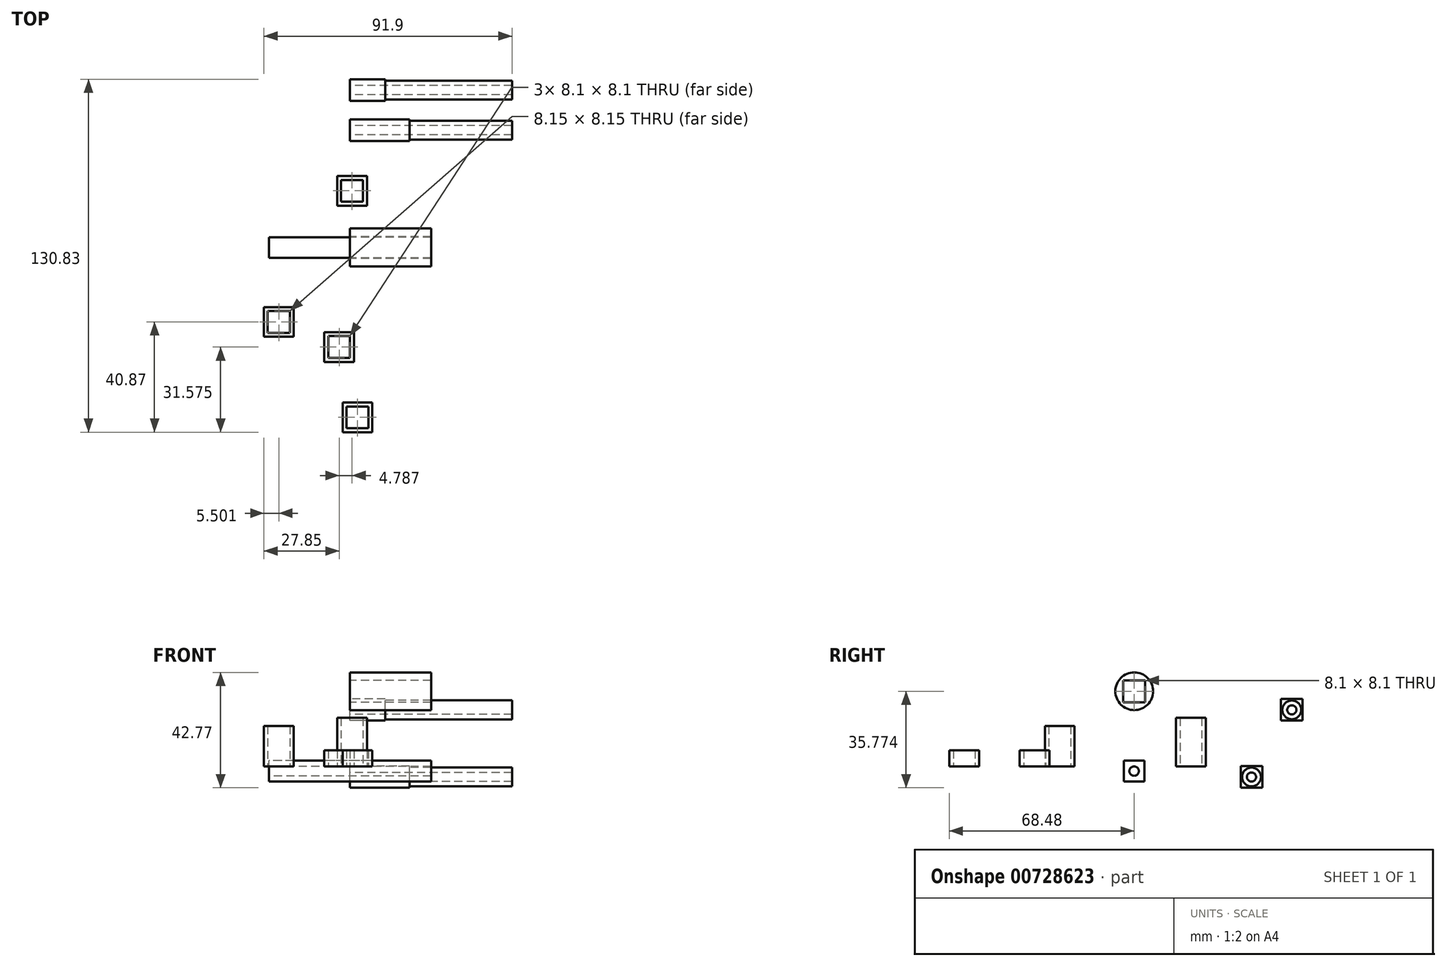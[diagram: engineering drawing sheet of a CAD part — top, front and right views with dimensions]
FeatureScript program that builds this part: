
annotation { "Feature Type Name" : "Feature", "Feature Type Description" : "" }
export const myFeature = defineFeature(function(context is Context, id is Id, definition is map)
    precondition{}
    {
        {
            var Q0;
            Q0=qCreatedBy(makeId("Right.planeOp"),FACE);
            var sketch = newSketch(context, id + "F0", { "sketchPlane" : qUnion([Q0])});
            skLineSegment(sketch, "E0.bottom", {"start": v(3.85, -3.85) * mm, "end": v(-3.85, -3.85) * mm});
            skLineSegment(sketch, "E0.top", {"start": v(3.85, 3.85) * mm, "end": v(-3.85, 3.85) * mm});
            skLineSegment(sketch, "E0.left", {"start": v(3.85, -3.85) * mm, "end": v(3.85, 3.85) * mm});
            skLineSegment(sketch, "E0.right", {"start": v(-3.85, -3.85) * mm, "end": v(-3.85, 3.85) * mm});
            skPoint(sketch, "E0.middle", {"position": v(0, 0) * mm});
            skCircle(sketch, "E1", {"center": v(0, 0) * mm, "radius": 1.75 * mm});
            skCircle(sketch, "E2", {"center": v(43.48, -2.18) * mm, "radius": 1.7 * mm});
            skLineSegment(sketch, "E3.bottom", {"start": v(47.48, -6.18) * mm, "end": v(39.48, -6.18) * mm});
            skLineSegment(sketch, "E3.top", {"start": v(47.48, 1.82) * mm, "end": v(39.48, 1.82) * mm});
            skLineSegment(sketch, "E3.left", {"start": v(47.48, -6.18) * mm, "end": v(47.48, 1.82) * mm});
            skLineSegment(sketch, "E3.right", {"start": v(39.48, -6.18) * mm, "end": v(39.48, 1.82) * mm});
            skCircle(sketch, "E4", {"center": v(58.4, 22.7) * mm, "radius": 1.7 * mm});
            skLineSegment(sketch, "E5.bottom", {"start": v(62.4, 18.7) * mm, "end": v(54.4, 18.7) * mm});
            skLineSegment(sketch, "E5.top", {"start": v(62.4, 26.7) * mm, "end": v(54.4, 26.7) * mm});
            skLineSegment(sketch, "E5.left", {"start": v(62.4, 18.7) * mm, "end": v(62.4, 26.7) * mm});
            skLineSegment(sketch, "E5.right", {"start": v(54.4, 18.7) * mm, "end": v(54.4, 26.7) * mm});
            skSolve(sketch);
        }
        {
            var Q0;
            Q0=makeQuery(id+"F0.imprint","IMPRINT",FACE,{"disambiguationData":[TD([[makeQuery(id+"F0.imprint","IMPRINT",EDGE,{"derivedFrom":sQuery(id+"F0.wireOp",EDGE,"E0.bottom")}),-1.0]])]});
            extrude(context, id + "F1", {"entities" : qUnion([Q0]), "endBound" : BoundingType.SYMMETRIC, "depth" : 60 * mm, "offsetDistance" : 25 * mm});
        }
        {
            var Q0;
            Q0=qCreatedBy(makeId("Right.planeOp"),FACE);
            var sketch = newSketch(context, id + "F2", { "sketchPlane" : qUnion([Q0])});
            skLineSegment(sketch, "E6.bottom", {"start": v(-32.8, 1.71) * mm, "end": v(-40.9, 1.71) * mm});
            skLineSegment(sketch, "E6.top", {"start": v(-32.8, 9.81) * mm, "end": v(-40.9, 9.81) * mm});
            skLineSegment(sketch, "E6.left", {"start": v(-32.8, 1.71) * mm, "end": v(-32.8, 9.81) * mm});
            skLineSegment(sketch, "E6.right", {"start": v(-40.9, 1.71) * mm, "end": v(-40.9, 9.81) * mm});
            skPoint(sketch, "E6.middle", {"position": v(-36.86, 5.76) * mm});
            skLineSegment(sketch, "E7.bottom", {"start": v(-42.36, 0.26) * mm, "end": v(-31.36, 0.26) * mm});
            skLineSegment(sketch, "E7.top", {"start": v(-42.36, 11.26) * mm, "end": v(-31.36, 11.26) * mm});
            skLineSegment(sketch, "E7.left", {"start": v(-42.36, 0.26) * mm, "end": v(-42.36, 11.26) * mm});
            skLineSegment(sketch, "E7.right", {"start": v(-31.36, 0.26) * mm, "end": v(-31.36, 11.26) * mm});
            skSolve(sketch);
        }
        {
            var Q0;
            Q0 = qSketchRegion(id + "F2", true);
            extrude(context, id + "F3", {"entities" : qUnion([Q0]), "depth" : 6 * mm, "offsetDistance" : 25 * mm});
        }
        {
            var Q0;
            Q0=qCreatedBy(makeId("Right.planeOp"),FACE);
            var sketch = newSketch(context, id + "F4", { "sketchPlane" : qUnion([Q0])});
            skLineSegment(sketch, "E8.bottom", {"start": v(25.07, -3.07) * mm, "end": v(16.97, -3.07) * mm});
            skLineSegment(sketch, "E8.top", {"start": v(25.07, 5.03) * mm, "end": v(16.97, 5.03) * mm});
            skLineSegment(sketch, "E8.left", {"start": v(25.07, -3.07) * mm, "end": v(25.07, 5.03) * mm});
            skLineSegment(sketch, "E8.right", {"start": v(16.97, -3.07) * mm, "end": v(16.97, 5.03) * mm});
            skPoint(sketch, "E8.middle", {"position": v(21.02, 0.98) * mm});
            skLineSegment(sketch, "E9.bottom", {"start": v(15.52, -4.52) * mm, "end": v(26.52, -4.52) * mm});
            skLineSegment(sketch, "E9.top", {"start": v(15.52, 6.48) * mm, "end": v(26.52, 6.48) * mm});
            skLineSegment(sketch, "E9.left", {"start": v(15.52, -4.52) * mm, "end": v(15.52, 6.48) * mm});
            skLineSegment(sketch, "E9.right", {"start": v(26.52, -4.52) * mm, "end": v(26.52, 6.48) * mm});
            skSolve(sketch);
        }
        {
            var Q0;
            Q0 = qSketchRegion(id + "F4", true);
            extrude(context, id + "F5", {"entities" : qUnion([Q0]), "depth" : 18 * mm, "offsetDistance" : 25 * mm});
        }
        {
            var Q0;
            Q0=qCreatedBy(makeId("Right.planeOp"),FACE);
            var sketch = newSketch(context, id + "F6", { "sketchPlane" : qUnion([Q0])});
            skLineSegment(sketch, "E10.bottom", {"start": v(-58.88, -5.07) * mm, "end": v(-66.98, -5.07) * mm});
            skLineSegment(sketch, "E10.top", {"start": v(-58.88, 3.03) * mm, "end": v(-66.98, 3.03) * mm});
            skLineSegment(sketch, "E10.left", {"start": v(-58.88, -5.07) * mm, "end": v(-58.88, 3.03) * mm});
            skLineSegment(sketch, "E10.right", {"start": v(-66.98, -5.07) * mm, "end": v(-66.98, 3.03) * mm});
            skPoint(sketch, "E10.middle", {"position": v(-62.93, -1.02) * mm});
            skLineSegment(sketch, "E11.bottom", {"start": v(-68.43, -6.52) * mm, "end": v(-57.43, -6.52) * mm});
            skLineSegment(sketch, "E11.top", {"start": v(-68.43, 4.48) * mm, "end": v(-57.43, 4.48) * mm});
            skLineSegment(sketch, "E11.left", {"start": v(-68.43, -6.52) * mm, "end": v(-68.43, 4.48) * mm});
            skLineSegment(sketch, "E11.right", {"start": v(-57.43, -6.52) * mm, "end": v(-57.43, 4.48) * mm});
            skSolve(sketch);
        }
        {
            var Q0;
            Q0 = qSketchRegion(id + "F6", true);
            extrude(context, id + "F7", {"entities" : qUnion([Q0]), "depth" : 6 * mm, "offsetDistance" : 25 * mm});
        }
        {
            var Q0;
            Q0=qCreatedBy(makeId("Right.planeOp"),FACE);
            var sketch = newSketch(context, id + "F8", { "sketchPlane" : qUnion([Q0])});
            skLineSegment(sketch, "E12.bottom", {"start": v(-23.48, 24.04) * mm, "end": v(-31.63, 24.04) * mm});
            skLineSegment(sketch, "E12.top", {"start": v(-23.48, 32.19) * mm, "end": v(-31.63, 32.19) * mm});
            skLineSegment(sketch, "E12.left", {"start": v(-23.48, 24.04) * mm, "end": v(-23.48, 32.19) * mm});
            skLineSegment(sketch, "E12.right", {"start": v(-31.63, 24.04) * mm, "end": v(-31.63, 32.19) * mm});
            skPoint(sketch, "E12.middle", {"position": v(-27.56, 28.11) * mm});
            skLineSegment(sketch, "E13.bottom", {"start": v(-22.06, 22.61) * mm, "end": v(-33.06, 22.61) * mm});
            skLineSegment(sketch, "E13.top", {"start": v(-22.06, 33.61) * mm, "end": v(-33.06, 33.61) * mm});
            skLineSegment(sketch, "E13.left", {"start": v(-22.06, 22.61) * mm, "end": v(-22.06, 33.61) * mm});
            skLineSegment(sketch, "E13.right", {"start": v(-33.06, 22.61) * mm, "end": v(-33.06, 33.61) * mm});
            skSolve(sketch);
        }
        {
            var Q0;
            Q0 = qSketchRegion(id + "F8", true);
            extrude(context, id + "F9", {"entities" : qUnion([Q0]), "depth" : 15 * mm, "offsetDistance" : 25 * mm});
        }
        {
            var Q0;
            Q0=qCreatedBy(makeId("Right.planeOp"),FACE);
            var sketch = newSketch(context, id + "F10", { "sketchPlane" : qUnion([Q0])});
            skCircle(sketch, "E14", {"center": v(43.48, -2.18) * mm, "radius": 1.7 * mm});
            skCircle(sketch, "E15", {"center": v(43.48, -2.18) * mm, "radius": 3.5 * mm});
            skCircle(sketch, "E16", {"center": v(58.4, 22.7) * mm, "radius": 1.7 * mm});
            skCircle(sketch, "E17", {"center": v(58.4, 22.7) * mm, "radius": 3.5 * mm});
            skSolve(sketch);
        }
        {
            var Q0;
            Q0=makeQuery(id+"F0.imprint","IMPRINT",FACE,{"disambiguationData":[TD([[makeQuery(id+"F0.imprint","IMPRINT",EDGE,{"derivedFrom":sQuery(id+"F0.wireOp",EDGE,"E2")}),-1.0]])]});
            extrude(context, id + "F11", {"entities" : qUnion([Q0]), "operationType" : NewBodyOperationType.ADD, "depth" : 22 * mm, "offsetDistance" : 25 * mm});
        }
        {
            var Q0;
            Q0=makeQuery(id+"F10.imprint","IMPRINT",FACE,{"disambiguationData":[TD([[makeQuery(id+"F10.imprint","IMPRINT",EDGE,{"derivedFrom":sQuery(id+"F10.wireOp",EDGE,"E14")}),-1.0]])]});
            extrude(context, id + "F12", {"entities" : qUnion([Q0]), "operationType" : NewBodyOperationType.ADD, "depth" : (38 + 22) * mm, "offsetDistance" : 25 * mm, "hasSecondDirection" : true, "secondDirectionOppositeDirection" : false, "secondDirectionDepth" : 22 * mm});
        }
        {
            var Q0;
            Q0=qCreatedBy(makeId("Right.planeOp"),FACE);
            var sketch = newSketch(context, id + "F13", { "sketchPlane" : qUnion([Q0])});
            skLineSegment(sketch, "E18.bottom", {"start": v(4.1, 25.54) * mm, "end": v(-4, 25.54) * mm});
            skLineSegment(sketch, "E18.top", {"start": v(4.1, 33.64) * mm, "end": v(-4, 33.64) * mm});
            skLineSegment(sketch, "E18.left", {"start": v(4.1, 25.54) * mm, "end": v(4.1, 33.64) * mm});
            skLineSegment(sketch, "E18.right", {"start": v(-4, 25.54) * mm, "end": v(-4, 33.64) * mm});
            skPoint(sketch, "E18.middle", {"position": v(0.05, 29.6) * mm});
            skCircle(sketch, "E19", {"center": v(0.05, 29.6) * mm, "radius": 7 * mm});
            skSolve(sketch);
        }
        {
            var Q0;
            Q0 = qSketchRegion(id + "F13", true);
            extrude(context, id + "F14", {"entities" : qUnion([Q0]), "depth" : 30 * mm, "offsetDistance" : 25 * mm});
        }
        {
            var Q0;
            Q0=makeQuery(id+"F0.imprint","IMPRINT",FACE,{"disambiguationData":[TD([[makeQuery(id+"F0.imprint","IMPRINT",EDGE,{"derivedFrom":sQuery(id+"F0.wireOp",EDGE,"E4")}),-1.0]])]});
            extrude(context, id + "F15", {"entities" : qUnion([Q0]), "depth" : 13 * mm, "offsetDistance" : 25 * mm});
        }
        {
            var Q0;
            Q0=makeQuery(id+"F10.imprint","IMPRINT",FACE,{"disambiguationData":[TD([[makeQuery(id+"F10.imprint","IMPRINT",EDGE,{"derivedFrom":sQuery(id+"F10.wireOp",EDGE,"E16")}),-1.0]])]});
            extrude(context, id + "F16", {"entities" : qUnion([Q0]), "operationType" : NewBodyOperationType.ADD, "depth" : (38 + 9 + 13) * mm, "offsetDistance" : 25 * mm, "hasSecondDirection" : true, "secondDirectionOppositeDirection" : false, "secondDirectionDepth" : 13 * mm});
        }
        {
            var Q0;
            Q0=makeQuery(id+"F9.opExtrude","SWEPT_BODY",BODY,{"disambiguationData":[OSD([sQuery(id+"F8.wireOp",EDGE,"E12.bottom"),sQuery(id+"F8.wireOp",EDGE,"E12.top"),sQuery(id+"F8.wireOp",EDGE,"E12.left"),sQuery(id+"F8.wireOp",EDGE,"E12.right"),sQuery(id+"F8.wireOp",EDGE,"E13.bottom"),sQuery(id+"F8.wireOp",EDGE,"E13.top"),sQuery(id+"F8.wireOp",EDGE,"E13.left"),sQuery(id+"F8.wireOp",EDGE,"E13.right")])]});
            var Q1;
            Q1=makeQuery(id+"F7.opExtrude","SWEPT_BODY",BODY,{"disambiguationData":[OSD([sQuery(id+"F6.wireOp",EDGE,"E10.bottom"),sQuery(id+"F6.wireOp",EDGE,"E10.top"),sQuery(id+"F6.wireOp",EDGE,"E10.left"),sQuery(id+"F6.wireOp",EDGE,"E10.right"),sQuery(id+"F6.wireOp",EDGE,"E11.bottom"),sQuery(id+"F6.wireOp",EDGE,"E11.top"),sQuery(id+"F6.wireOp",EDGE,"E11.left"),sQuery(id+"F6.wireOp",EDGE,"E11.right")])]});
            var Q2;
            Q2=makeQuery(id+"F3.opExtrude","SWEPT_BODY",BODY,{"disambiguationData":[OSD([sQuery(id+"F2.wireOp",EDGE,"E6.bottom"),sQuery(id+"F2.wireOp",EDGE,"E6.top"),sQuery(id+"F2.wireOp",EDGE,"E6.left"),sQuery(id+"F2.wireOp",EDGE,"E6.right"),sQuery(id+"F2.wireOp",EDGE,"E7.bottom"),sQuery(id+"F2.wireOp",EDGE,"E7.top"),sQuery(id+"F2.wireOp",EDGE,"E7.left"),sQuery(id+"F2.wireOp",EDGE,"E7.right")])]});
            var Q3;
            Q3=makeQuery(id+"F5.opExtrude","SWEPT_BODY",BODY,{"disambiguationData":[OSD([sQuery(id+"F4.wireOp",EDGE,"E8.bottom"),sQuery(id+"F4.wireOp",EDGE,"E8.top"),sQuery(id+"F4.wireOp",EDGE,"E8.left"),sQuery(id+"F4.wireOp",EDGE,"E8.right"),sQuery(id+"F4.wireOp",EDGE,"E9.bottom"),sQuery(id+"F4.wireOp",EDGE,"E9.top"),sQuery(id+"F4.wireOp",EDGE,"E9.left"),sQuery(id+"F4.wireOp",EDGE,"E9.right")])]});
            var Q4;
            Q4=makeQuery(id+"F3.opExtrude","CAP_EDGE",EDGE,{"disambiguationData":[OSD([sQuery(id+"F2.wireOp",EDGE,"E6.bottom")])],"isStart":true});
            var Q5;
            Q5=makeQuery(id+"F3.opExtrude","CAP_EDGE",EDGE,{"disambiguationData":[OSD([sQuery(id+"F2.wireOp",EDGE,"E6.bottom")])],"isStart":true});
            transform(context, id + "F17", {"entities" : qUnion([Q0, Q1, Q2, Q3]), "transformType" : TransformType.ROTATION, "transformAxis" : qUnion([Q5]), "angle" : 90 * degree, "makeCopy" : false});
        }
    });
